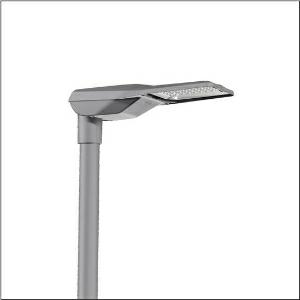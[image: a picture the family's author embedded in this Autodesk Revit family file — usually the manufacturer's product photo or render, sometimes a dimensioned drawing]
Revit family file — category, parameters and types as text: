
# Revit family: streetlight_sl_21_iq_mini___st0_5a_5xe2b31g08gb_b1a9
name_source: partatom
category: Lighting Fixtures
units: mm (PartAtom-declared; Revit-internal decimal feet)

## family parameters
Cut with Voids When Loaded = No
Host = Face
Light Source = No
Part Type = Normal
Room Calculation Point = No
Round Connector Dimension = Use Diameter
Shared = No

## types (1)
- --- (1 x LED, 5680 lm, 37.1 W, 3000K)
    Apparent Load = 37 VA
    CIE Flux Codes = 41 75 97 100 100
    Color Rendering = 70
    Color Temperature = 3000K
    Default Elevation = 1800 mm
    Description = Streetlight SL 21 iQ mini, mast luminaire, primary light control with lens, of PMMA, primary optical cover: cover, of toughened safety glass, transparent, light distribution: ST0.5a, light emission: direct distribution, primary light characteristic: asymmetric, installation type: post-top, side-entry, LED, High Power LED, rated luminous flux: 5.680lm, luminous efficacy: 153lm/W, light colour: 730, colour temperature: 3000K, control gear: iQ Street-Remote, control: Street-Remote, Auto-Match, Temp-Guard, Lumen-Switch, Night-Set, Smart-Wire, Light-Fading, Desk-Remote (wireless, voltage-free reading and setting of iQ features in the workshop via application-optimized NFC function/RFID function), optimised constant luminous flux control (CLO 2.0), pre-setting: linear dimming characteristic, mains connection: 220..240V, AC, 50/60Hz, start of lifetime: 37W, end of service life: 39W, reduction: 18W, luminaire housing, of diecast aluminium, powder-coated, Siteco® metallic grey (DB 702S), corrosivity category C5 mid according to DIN EN ISO 12944, please order mast flange separately, inclination adjustable: 0°, 5°, 10°, 15°, sealing non-destructively replaceable, multi-level sealing system, length: 628mm, width: 235mm, height: 110mm, mast flange for spigot size: 42mm (side-entry): 5XC10008XM4, 60/48mm (side-entry/post-top): 5XC10108XM2, 76/60mm (side-entry/post-top): 5XC10108XM1, mounting height: 4..8m, protection rating (complete): IP66, insulation class (complete): insulation class II (safety insulation), certification: CE, ENEC, ENEC+, VDE, impact resistance: IK10, permissible operating ambient temperature for outdoor applications: -40..+50°C, standard-compliant lighting for roads and squares, packaging unit: 1 piece

Light Distribution: ST0.5a
    Height = 110 mm
    Lamp = 1 x LED
    Lamp Light Flux = 5680 lm
    Lamp Power = 37.1 W
    Lamp count = 1
    Length = 625 mm
    Luminous efficacy = 153 lm/W
    Manufacturer = Siteco
    ModVariant = No
    Model = 5XE2B31G08GB
    Number of Poles = 1
    OnlyDefault = Yes
    Power Factor = 1
    Product Name = Streetlight SL 21 iQ mini | ST0.5a
    Product group = mast luminaire | pylon top
    ProductGroupID = 6100
    Protection Class = Protection class II
    Protection Degree = IP 66
    RLX_Detail_Level = 1
    RLX_Emergency_Light_Flux = 0 lm
    RLX_Emergency_Type = 0
    RLX_Emergency_Type_DB = No
    RlxData = <blob elided: 37317 chars, md5=f838b639>
    Socket = socket
    Standby Power = 0 W
    System Light Flux = 5680 lm
    System Power = 37 W
    Type Comments = factory setting: luminous flux: 100 % | dim-lin: 254 | 385 mA
    Type Image = l_1003519.jpg
    URL = http://relux.com
    VarID = @adj_191374
    Voltage = 0 V
    Weight = 0.00 kg
    Width = 234 mm

## geometry (parser evidence)
native form markers: Blend x4, Sweep x11
no freeform markers — native parametric forms only
